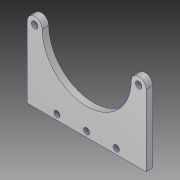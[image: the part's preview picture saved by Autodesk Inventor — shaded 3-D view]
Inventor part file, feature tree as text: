
AUTODESK INVENTOR PART (.ipt)
format: ipt  version: 2019 (Build 230136000, 136)  size: 109,568 bytes
history: native  units: mm
features: extrude x1, sketch x1
ambient origin geometry x8: Origin, YZ Plane, XZ Plane, XY Plane, X Axis, Y Axis, Z Axis, Center Point
bodies: Body1 (feature_tree)
feature tree (2):
  extrude  "Extrusion2"  Depth=6.0mm
  sketch  "Sketch1"  dims[d0=108.0mm d2=6.0mm d3=6.0mm d6=94.5mm d9=65.0mm d21=5.0mm d23=5.5mm d24=5.5mm d25=5.5mm d26=54.0mm d27=6.0mm d28=0.0mm]
